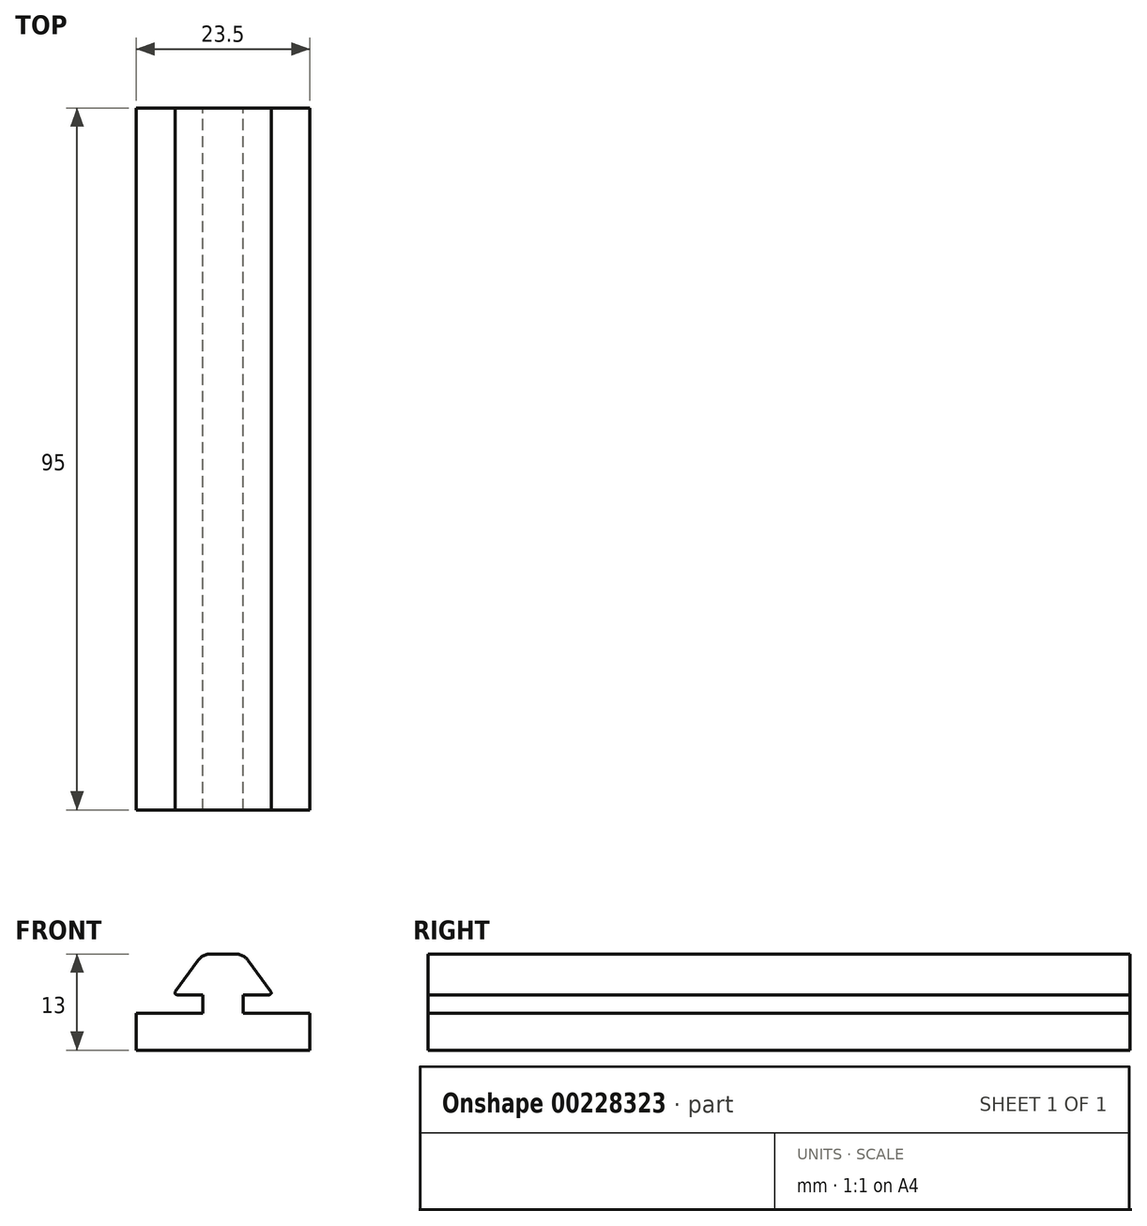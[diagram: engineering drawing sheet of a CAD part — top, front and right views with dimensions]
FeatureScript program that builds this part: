
annotation { "Feature Type Name" : "Feature", "Feature Type Description" : "" }
export const myFeature = defineFeature(function(context is Context, id is Id, definition is map)
    precondition{}
    {
        {
            var Q0;
            Q0=qCreatedBy(makeId("Front.planeOp"),FACE);
            var sketch = newSketch(context, id + "F0", { "sketchPlane" : qUnion([Q0])});
            skLineSegment(sketch, "E0", {"start": v(-6.75, 0) * mm, "end": v(6.75, 0) * mm});
            skLineSegment(sketch, "E1", {"start": v(0, 0) * mm, "end": v(0, 5.5) * mm});
            skLineSegment(sketch, "E2", {"start": v(0, 5.5) * mm, "end": v(-2.75, 5.5) * mm});
            skLineSegment(sketch, "E3", {"start": v(-2.75, 5.5) * mm, "end": v(2.75, 5.5) * mm});
            skLineSegment(sketch, "E4", {"start": v(-6.75, 0) * mm, "end": v(-2.75, 5.5) * mm});
            skLineSegment(sketch, "E5", {"start": v(2.75, 5.5) * mm, "end": v(6.75, 0) * mm});
            skLineSegment(sketch, "E6", {"start": v(-2.75, 5.5) * mm, "end": v(-2.75, -2.5) * mm});
            skLineSegment(sketch, "E7", {"start": v(2.75, 5.5) * mm, "end": v(2.75, -2.5) * mm});
            skLineSegment(sketch, "E8", {"start": v(-2.75, -2.5) * mm, "end": v(-6.75, -2.5) * mm});
            skLineSegment(sketch, "E9", {"start": v(-6.75, -2.5) * mm, "end": v(-6.75, -7.5) * mm});
            skLineSegment(sketch, "E10", {"start": v(2.75, -2.5) * mm, "end": v(6.75, -2.5) * mm});
            skLineSegment(sketch, "E11", {"start": v(-6.75, -7.5) * mm, "end": v(6.75, -7.5) * mm});
            skLineSegment(sketch, "E12", {"start": v(6.75, -2.5) * mm, "end": v(6.75, -7.5) * mm});
            skSolve(sketch);
        }
        {
            var Q0;
            {var subQ0=sQuery(id+"F0.wireOp",EDGE,"E1");Q0=makeQuery(id+"F0.imprint","IMPRINT",FACE,{"disambiguationData":[TD([[makeQuery(id+"F0.imprint","IMPRINT",EDGE,{"derivedFrom":subQ0}),-1.0]])]});}
            var Q1;
            {var subQ4=sQuery(id+"F0.wireOp",EDGE,"E8");Q1=makeQuery(id+"F0.imprint","IMPRINT",FACE,{"disambiguationData":[TD([[makeQuery(id+"F0.imprint","IMPRINT",EDGE,{"derivedFrom":subQ4}),1.0]])]});}
            var Q2;
            {var subQ0=sQuery(id+"F0.wireOp",EDGE,"E5");Q2=makeQuery(id+"F0.imprint","IMPRINT",FACE,{"disambiguationData":[TD([[makeQuery(id+"F0.imprint","IMPRINT",EDGE,{"derivedFrom":subQ0}),-1.0]])]});}
            var Q3;
            {var subQ0=sQuery(id+"F0.wireOp",EDGE,"E1");Q3=makeQuery(id+"F0.imprint","IMPRINT",FACE,{"disambiguationData":[TD([[makeQuery(id+"F0.imprint","IMPRINT",EDGE,{"derivedFrom":subQ0}),1.0]])]});}
            var Q4;
            {var subQ0=sQuery(id+"F0.wireOp",EDGE,"E4");Q4=makeQuery(id+"F0.imprint","IMPRINT",FACE,{"disambiguationData":[TD([[makeQuery(id+"F0.imprint","IMPRINT",EDGE,{"derivedFrom":subQ0}),-1.0]])]});}
            extrude(context, id + "F1", {"entities" : qUnion([Q0, Q1, Q2, Q3, Q4]), "depth" : 95 * mm});
        }
        {
            var Q0;
            Q0=makeQuery(id+"F1.opExtrude","SWEPT_EDGE",EDGE,{"disambiguationData":[OSD([sQuery(id+"F0.wireOp",EDGE,"E3"),sQuery(id+"F0.wireOp",EDGE,"E5"),sQuery(id+"F0.wireOp",EDGE,"E7")])]});
            var Q1;
            Q1=makeQuery(id+"F1.opExtrude","SWEPT_EDGE",EDGE,{"disambiguationData":[OSD([sQuery(id+"F0.wireOp",EDGE,"E3"),sQuery(id+"F0.wireOp",EDGE,"E4"),sQuery(id+"F0.wireOp",EDGE,"E6")])]});
            fillet(context, id + "F2", {"entities" : qUnion([Q0, Q1]), "radius" : 2 * mm, "tangentPropagation" : true, "allowEdgeOverflow" : false});
        }
        {
            var Q0;
            Q0=makeQuery(id+"F1.opExtrude","SWEPT_EDGE",EDGE,{"disambiguationData":[OSD([sQuery(id+"F0.wireOp",EDGE,"E0"),sQuery(id+"F0.wireOp",EDGE,"E5")])]});
            var Q1;
            Q1=makeQuery(id+"F1.opExtrude","SWEPT_EDGE",EDGE,{"disambiguationData":[OSD([sQuery(id+"F0.wireOp",EDGE,"E0"),sQuery(id+"F0.wireOp",EDGE,"E4")])]});
            fillet(context, id + "F3", {"entities" : qUnion([Q0, Q1]), "radius" : .25 * mm, "tangentPropagation" : true, "allowEdgeOverflow" : false});
        }
        {
            var Q0;
            Q0=makeQuery(id+"F1.opExtrude","SWEPT_FACE",FACE,{"disambiguationData":[OSD([sQuery(id+"F0.wireOp",EDGE,"E9")])]});
            extrude(context, id + "F4", {"entities" : qUnion([Q0]), "operationType" : NewBodyOperationType.ADD, "depth" : 5 * mm});
        }
        {
            var Q0;
            Q0=makeQuery(id+"F1.opExtrude","SWEPT_FACE",FACE,{"disambiguationData":[OSD([sQuery(id+"F0.wireOp",EDGE,"E12")])]});
            extrude(context, id + "F5", {"entities" : qUnion([Q0]), "operationType" : NewBodyOperationType.ADD, "depth" : 5 * mm});
        }
    });
